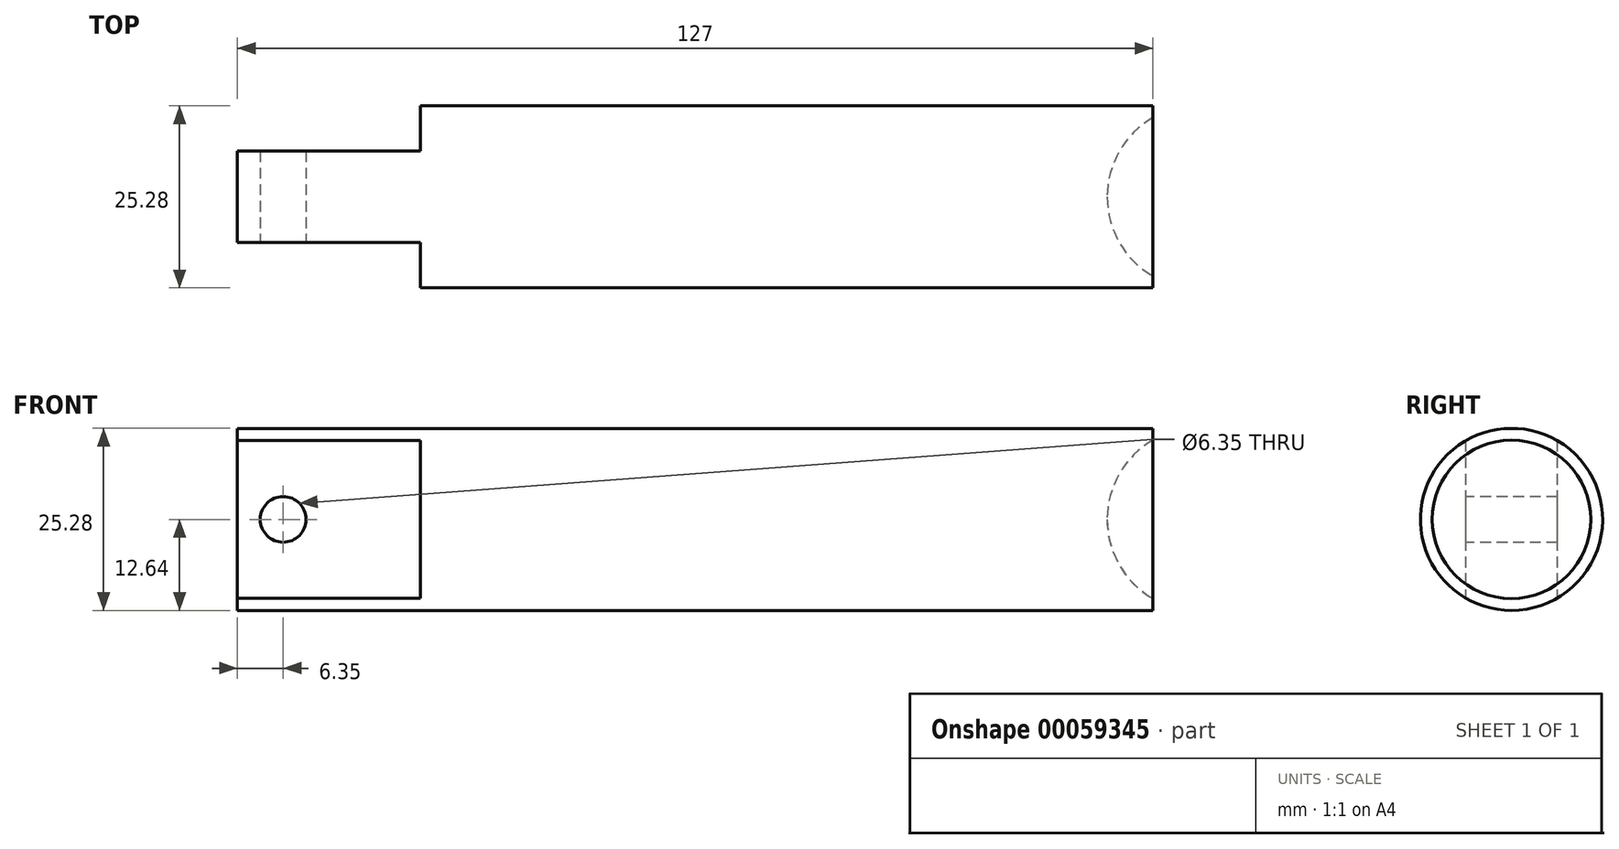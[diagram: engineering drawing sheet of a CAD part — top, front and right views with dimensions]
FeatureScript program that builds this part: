
annotation { "Feature Type Name" : "Feature", "Feature Type Description" : "" }
export const myFeature = defineFeature(function(context is Context, id is Id, definition is map)
    precondition{}
    {
        {
            var Q0;
            Q0=qCreatedBy(makeId("Right.planeOp"),FACE);
            var sketch = newSketch(context, id + "F0", { "sketchPlane" : qUnion([Q0])});
            skCircle(sketch, "E0", {"center": v(0, 0) * mm, "radius": 12.64 * mm});
            skSolve(sketch);
        }
        {
            var Q0;
            Q0 = qSketchRegion(id + "F0", true);
            extrude(context, id + "F1", {"entities" : qUnion([Q0]), "depth" : 127 * mm});
        }
        {
            var Q0;
            Q0=makeQuery(id+"F1.opExtrude","CAP_FACE",FACE,{"disambiguationData":[OSD([sQuery(id+"F0.wireOp",EDGE,"E0")])],"isStart":true});
            var sketch = newSketch(context, id + "F2", { "sketchPlane" : qUnion([Q0])});
            skLineSegment(sketch, "E1.bottom", {"start": v(6.35, 20.32) * mm, "end": v(26.67, 20.32) * mm});
            skLineSegment(sketch, "E1.top", {"start": v(6.35, -20.32) * mm, "end": v(26.67, -20.32) * mm});
            skLineSegment(sketch, "E1.left", {"start": v(6.35, 20.32) * mm, "end": v(6.35, -20.32) * mm});
            skLineSegment(sketch, "E1.right", {"start": v(26.67, 20.32) * mm, "end": v(26.67, -20.32) * mm});
            skLineSegment(sketch, "E2.MirrorCS", {"start": v(-26.67, 20.32) * mm, "end": v(-26.67, -20.32) * mm});
            skLineSegment(sketch, "E3.MirrorCS", {"start": v(-6.35, -20.32) * mm, "end": v(-26.67, -20.32) * mm});
            skLineSegment(sketch, "E4.MirrorCS", {"start": v(-6.35, 20.32) * mm, "end": v(-26.67, 20.32) * mm});
            skLineSegment(sketch, "E5.MirrorCS", {"start": v(-6.35, 20.32) * mm, "end": v(-6.35, -20.32) * mm});
            skSolve(sketch);
        }
        {
            var Q0;
            Q0 = qSketchRegion(id + "F2", true);
            extrude(context, id + "F3", {"entities" : qUnion([Q0]), "operationType" : NewBodyOperationType.REMOVE, "oppositeDirection" : true, "depth" : 25.4 * mm});
        }
        {
            var Q0;
            Q0=qCreatedBy(makeId("Front.planeOp"),FACE);
            var sketch = newSketch(context, id + "F4", { "sketchPlane" : qUnion([Q0])});
            skCircle(sketch, "E6", {"center": v(6.35, 0) * mm, "radius": 3.18 * mm});
            skSolve(sketch);
        }
        {
            var Q0;
            Q0 = qSketchRegion(id + "F4", true);
            extrude(context, id + "F5", {"entities" : qUnion([Q0]), "operationType" : NewBodyOperationType.REMOVE, "endBound" : BoundingType.SYMMETRIC, "oppositeDirection" : true, "depth" : 25.4 * mm});
        }
        {
            var Q0;
            Q0=qCreatedBy(makeId("Front.planeOp"),FACE);
            var sketch = newSketch(context, id + "F6", { "sketchPlane" : qUnion([Q0])});
            skArc(sketch, "E7", {"start": v(146.05, 0) * mm, "mid": v(133.35, 12.7) * mm, "end": v(120.65, 0) * mm});
            skLineSegment(sketch, "E8", {"start": v(120.65, 0) * mm, "end": v(146.05, 0) * mm});
            skSolve(sketch);
        }
        {
            var Q0;
            Q0=makeQuery(id+"F6.imprint","IMPRINT",FACE,{"disambiguationData":[TD([[makeQuery(id+"F6.imprint","IMPRINT",EDGE,{"derivedFrom":sQuery(id+"F6.wireOp",EDGE,"E7")}),1.0]])]});
            var Q1;
            Q1=sQuery(id+"F6.wireOp",EDGE,"E8");
            revolve(context, id + "F7", {"operationType" : NewBodyOperationType.REMOVE, "entities" : qUnion([Q0]), "axis" : qUnion([Q1]), "revolveType" : RevolveType.FULL, "oppositeDirection" : true});
        }
    });
